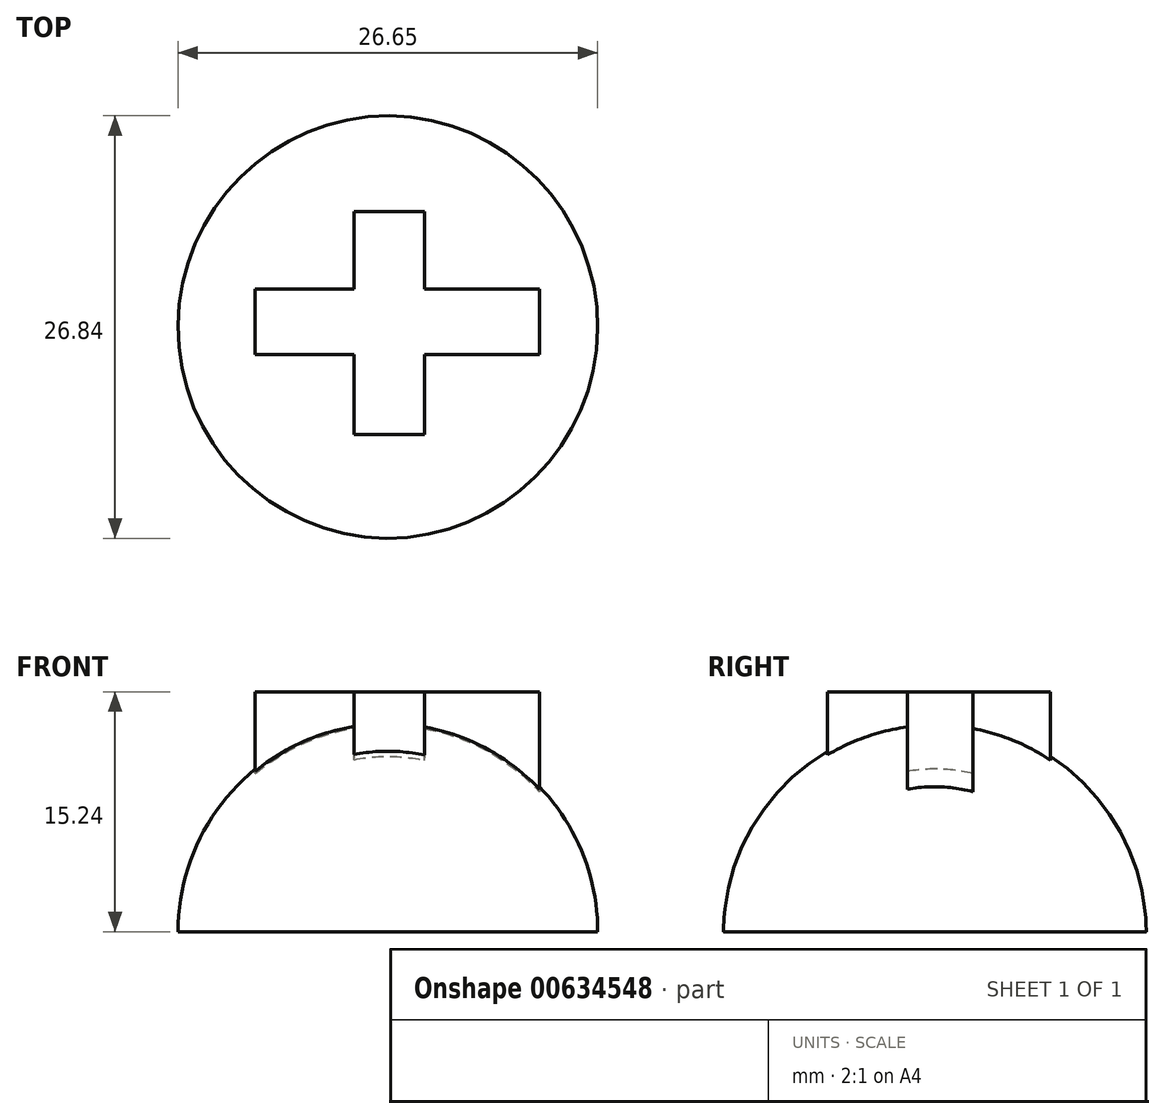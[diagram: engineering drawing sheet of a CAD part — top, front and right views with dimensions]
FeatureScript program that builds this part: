
annotation { "Feature Type Name" : "Feature", "Feature Type Description" : "" }
export const myFeature = defineFeature(function(context is Context, id is Id, definition is map)
    precondition{}
    {
        {
            var Q0;
            Q0=qCreatedBy(makeId("Top.planeOp"),FACE);
            var sketch = newSketch(context, id + "F0", { "sketchPlane" : qUnion([Q0])});
            skArc(sketch, "E0", {"start": v(0, -13.42) * mm, "mid": v(13.42, -0.1) * mm, "end": v(0.2, 13.42) * mm});
            skLineSegment(sketch, "E1", {"start": v(0.2, 13.42) * mm, "end": v(0, -13.42) * mm});
            skSolve(sketch);
        }
        {
            var Q0;
            Q0 = qSketchRegion(id + "F0", true);
            var Q1;
            Q1=sQuery(id+"F0.wireOp",EDGE,"E1");
            revolve(context, id + "F1", {"entities" : qUnion([Q0]), "axis" : qUnion([Q1]), "revolveType" : RevolveType.ONE_DIRECTION, "angle" : 180 * degree});
        }
        {
            var Q0;
            Q0=qCreatedBy(makeId("Top.planeOp"),FACE);
            var sketch = newSketch(context, id + "F2", { "sketchPlane" : qUnion([Q0])});
            skLineSegment(sketch, "E2.bottom", {"start": v(-2.06, 7.35) * mm, "end": v(2.42, 7.35) * mm});
            skLineSegment(sketch, "E2.top", {"start": v(-2.06, -6.82) * mm, "end": v(2.42, -6.82) * mm});
            skLineSegment(sketch, "E2.left", {"start": v(-2.06, 7.35) * mm, "end": v(-2.06, -6.82) * mm});
            skLineSegment(sketch, "E2.right", {"start": v(2.42, 7.35) * mm, "end": v(2.42, -6.82) * mm});
            skLineSegment(sketch, "E3.bottom", {"start": v(-8.32, 2.42) * mm, "end": v(9.73, 2.42) * mm});
            skLineSegment(sketch, "E3.top", {"start": v(-8.32, -1.75) * mm, "end": v(9.73, -1.75) * mm});
            skLineSegment(sketch, "E3.left", {"start": v(-8.32, 2.42) * mm, "end": v(-8.32, -1.75) * mm});
            skLineSegment(sketch, "E3.right", {"start": v(9.73, 2.42) * mm, "end": v(9.73, -1.75) * mm});
            skSolve(sketch);
        }
        {
            var Q0;
            Q0 = qSketchRegion(id + "F2", true);
            extrude(context, id + "F3", {"entities" : qUnion([Q0]), "operationType" : NewBodyOperationType.ADD, "depth" : 15.24 * mm, "offsetDistance" : 25.4 * mm});
        }
    });
